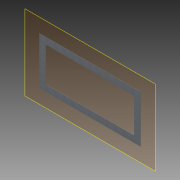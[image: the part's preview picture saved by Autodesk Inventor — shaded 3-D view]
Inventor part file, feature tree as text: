
AUTODESK INVENTOR PART (.ipt)
format: ipt  version: 2013 (Build 170138000, 138)  size: 79,872 bytes
history: native  units: in
note: dims shown in document units (in); Inventor stores cm internally (conversion verified against a paired STEP export)
features: reference x4, plane x1, extrude x1, sketch x1
ambient origin geometry x8: Origin, YZ Plane, XZ Plane, XY Plane, X Axis, Y Axis, Z Axis, Center Point
bodies: Solid1 (feature_tree)
feature tree (7):
  plane  "Work Plane1"
  extrude  "Extrusion1"  Depth=0.1in TaperAngle=0.0deg
  sketch  "Sketch1"  dims[d0=4.0in d1=0.1in d2=0.0in]
  reference  "Reference1"
  reference  "Reference2"
  reference  "Reference3"
  reference  "Reference4"
